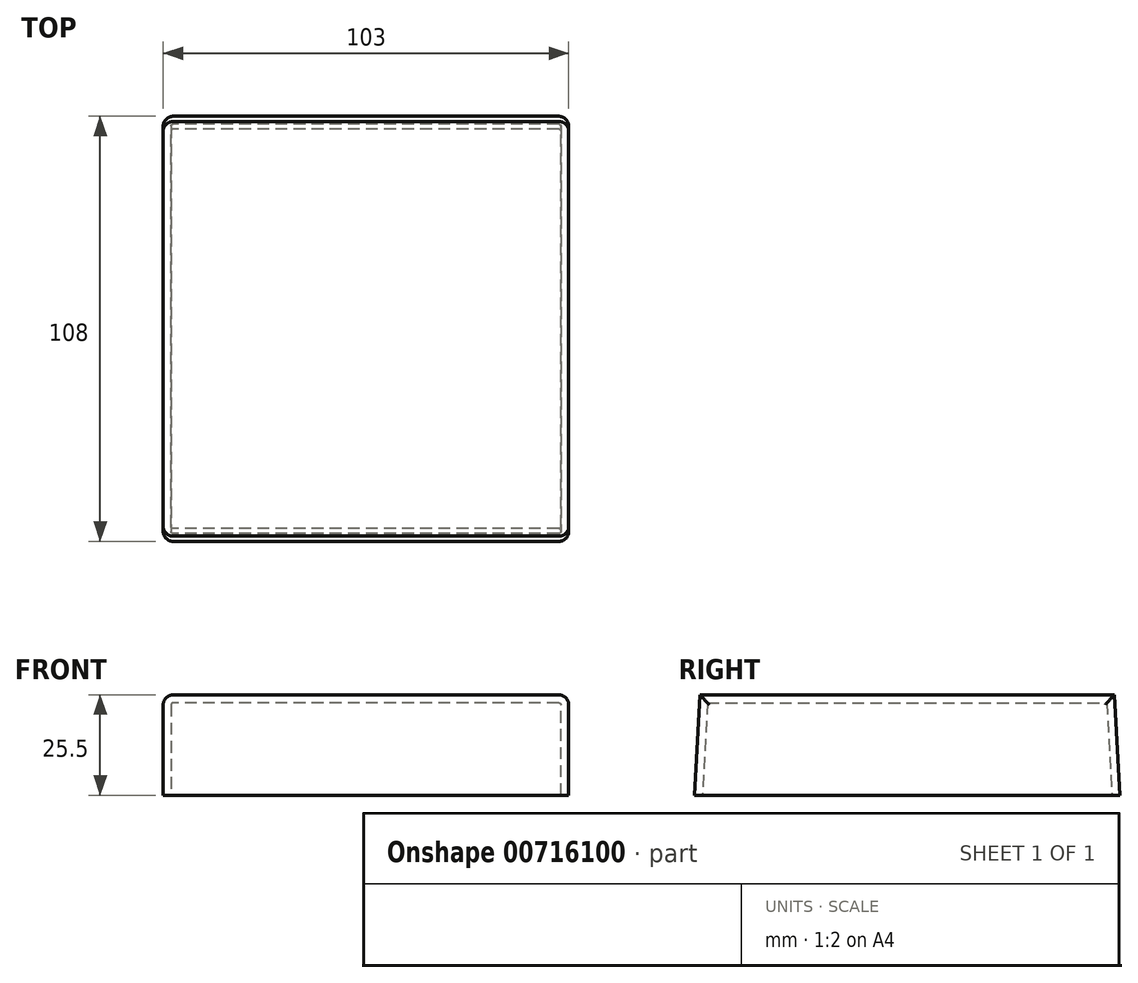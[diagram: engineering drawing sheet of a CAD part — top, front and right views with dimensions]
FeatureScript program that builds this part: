
annotation { "Feature Type Name" : "Feature", "Feature Type Description" : "" }
export const myFeature = defineFeature(function(context is Context, id is Id, definition is map)
    precondition{}
    {
        {
            var Q0;
            Q0=qCreatedBy(makeId("Top.planeOp"),FACE);
            var sketch = newSketch(context, id + "F0", { "sketchPlane" : qUnion([Q0])});
            skLineSegment(sketch, "E0.bottom", {"start": v(-51.5, 54) * mm, "end": v(51.5, 54) * mm});
            skLineSegment(sketch, "E0.top", {"start": v(-51.5, -54) * mm, "end": v(51.5, -54) * mm});
            skLineSegment(sketch, "E0.left", {"start": v(-51.5, 54) * mm, "end": v(-51.5, -54) * mm});
            skLineSegment(sketch, "E0.right", {"start": v(51.5, 54) * mm, "end": v(51.5, -54) * mm});
            skSolve(sketch);
        }
        {
            var Q0;
            Q0=qCreatedBy(makeId("Front.planeOp"),FACE);
            var sketch = newSketch(context, id + "F1", { "sketchPlane" : qUnion([Q0])});
            skLineSegment(sketch, "E1.bottom", {"start": v(-51.5, 0) * mm, "end": v(51.5, 0) * mm});
            skLineSegment(sketch, "E1.top", {"start": v(-51.5, 25.5) * mm, "end": v(51.5, 25.5) * mm});
            skLineSegment(sketch, "E1.left", {"start": v(-51.5, 0) * mm, "end": v(-51.5, 25.5) * mm});
            skLineSegment(sketch, "E1.right", {"start": v(51.5, 0) * mm, "end": v(51.5, 25.5) * mm});
            skSolve(sketch);
        }
        {
            var Q0;
            Q0=qCreatedBy(makeId("Right.planeOp"),FACE);
            var sketch = newSketch(context, id + "F2", { "sketchPlane" : qUnion([Q0])});
            skLineSegment(sketch, "E2", {"start": v(54, 0) * mm, "end": v(52.66, 25.5) * mm});
            skLineSegment(sketch, "E3", {"start": v(52.66, 25.5) * mm, "end": v(-52.66, 25.5) * mm});
            skLineSegment(sketch, "E4.MirrorCS", {"start": v(-54, 0) * mm, "end": v(-52.66, 25.5) * mm});
            skLineSegment(sketch, "E5", {"start": v(54, 0) * mm, "end": v(-54, 0) * mm});
            skSolve(sketch);
        }
        {
            var Q0;
            Q0=makeQuery(id+"F2.imprint","IMPRINT",FACE,{"disambiguationData":[TD([[makeQuery(id+"F2.imprint","IMPRINT",EDGE,{"derivedFrom":sQuery(id+"F2.wireOp",EDGE,"E2")}),1.0]])]});
            var Q1;
            Q1=sQuery(id+"F0.wireOp",VERTEX,"E0.right.end");
            var Q2;
            Q2=sQuery(id+"F0.wireOp",VERTEX,"E0.left.end");
            extrude(context, id + "F3", {"entities" : qUnion([Q0]), "endBound" : BoundingType.UP_TO_VERTEX, "depth" : 25 * mm, "endBoundEntityVertex" : qUnion([Q1]), "offsetDistance" : 25 * mm, "hasSecondDirection" : true, "secondDirectionBound" : SecondDirectionBoundingType.UP_TO_VERTEX, "secondDirectionOppositeDirection" : true, "secondDirectionDepth" : 25 * mm, "secondDirectionBoundEntityVertex" : qUnion([Q2])});
        }
        {
            var Q0;
            Q0=makeQuery(id+"F3.opExtrude","TWEAK_EDGE",EDGE,{"derivedFrom":[makeQuery(id+"F2.imprint","IMPRINT",EDGE,{"derivedFrom":sQuery(id+"F2.wireOp",EDGE,"E3")}),makeQuery(id+"F2.imprint","IMPRINT",EDGE,{"derivedFrom":sQuery(id+"F2.wireOp",EDGE,"E4.MirrorCS")})]});
            var Q1;
            Q1=makeQuery(id+"F3.opExtrude","CAP_EDGE",EDGE,{"disambiguationData":[OSD([sQuery(id+"F2.wireOp",EDGE,"E4.MirrorCS")])],"isStart":true});
            var Q2;
            Q2=makeQuery(id+"F3.opExtrude","CAP_EDGE",EDGE,{"disambiguationData":[OSD([sQuery(id+"F2.wireOp",EDGE,"E3")])],"isStart":true});
            var Q3;
            Q3=makeQuery(id+"F3.opExtrude","CAP_EDGE",EDGE,{"disambiguationData":[OSD([sQuery(id+"F2.wireOp",EDGE,"E3")])],"isStart":false});
            var Q4;
            Q4=makeQuery(id+"F3.opExtrude","CAP_EDGE",EDGE,{"disambiguationData":[OSD([sQuery(id+"F2.wireOp",EDGE,"E4.MirrorCS")])],"isStart":false});
            var Q5;
            Q5=makeQuery(id+"F3.opExtrude","CAP_EDGE",EDGE,{"disambiguationData":[OSD([sQuery(id+"F2.wireOp",EDGE,"E2")])],"isStart":false});
            var Q6;
            Q6=makeQuery(id+"F3.opExtrude","TWEAK_EDGE",EDGE,{"derivedFrom":[makeQuery(id+"F2.imprint","IMPRINT",EDGE,{"derivedFrom":sQuery(id+"F2.wireOp",EDGE,"E2")}),makeQuery(id+"F2.imprint","IMPRINT",EDGE,{"derivedFrom":sQuery(id+"F2.wireOp",EDGE,"E3")})]});
            var Q7;
            Q7=makeQuery(id+"F3.opExtrude","CAP_EDGE",EDGE,{"disambiguationData":[OSD([sQuery(id+"F2.wireOp",EDGE,"E2")])],"isStart":true});
            fillet(context, id + "F4", {"entities" : qUnion([Q0, Q1, Q2, Q3, Q4, Q5, Q6, Q7]), "radius" : 2.5 * mm, "tangentPropagation" : true, "allowEdgeOverflow" : false});
        }
        {
            var Q0;
            Q0=makeQuery(id+"F3.opExtrude","SWEPT_FACE",FACE,{"disambiguationData":[OSD([sQuery(id+"F2.wireOp",EDGE,"E5")])]});
            shell(context, id + "F5", {"entities" : qUnion([Q0]), "thickness" : 2 * mm});
        }
    });
